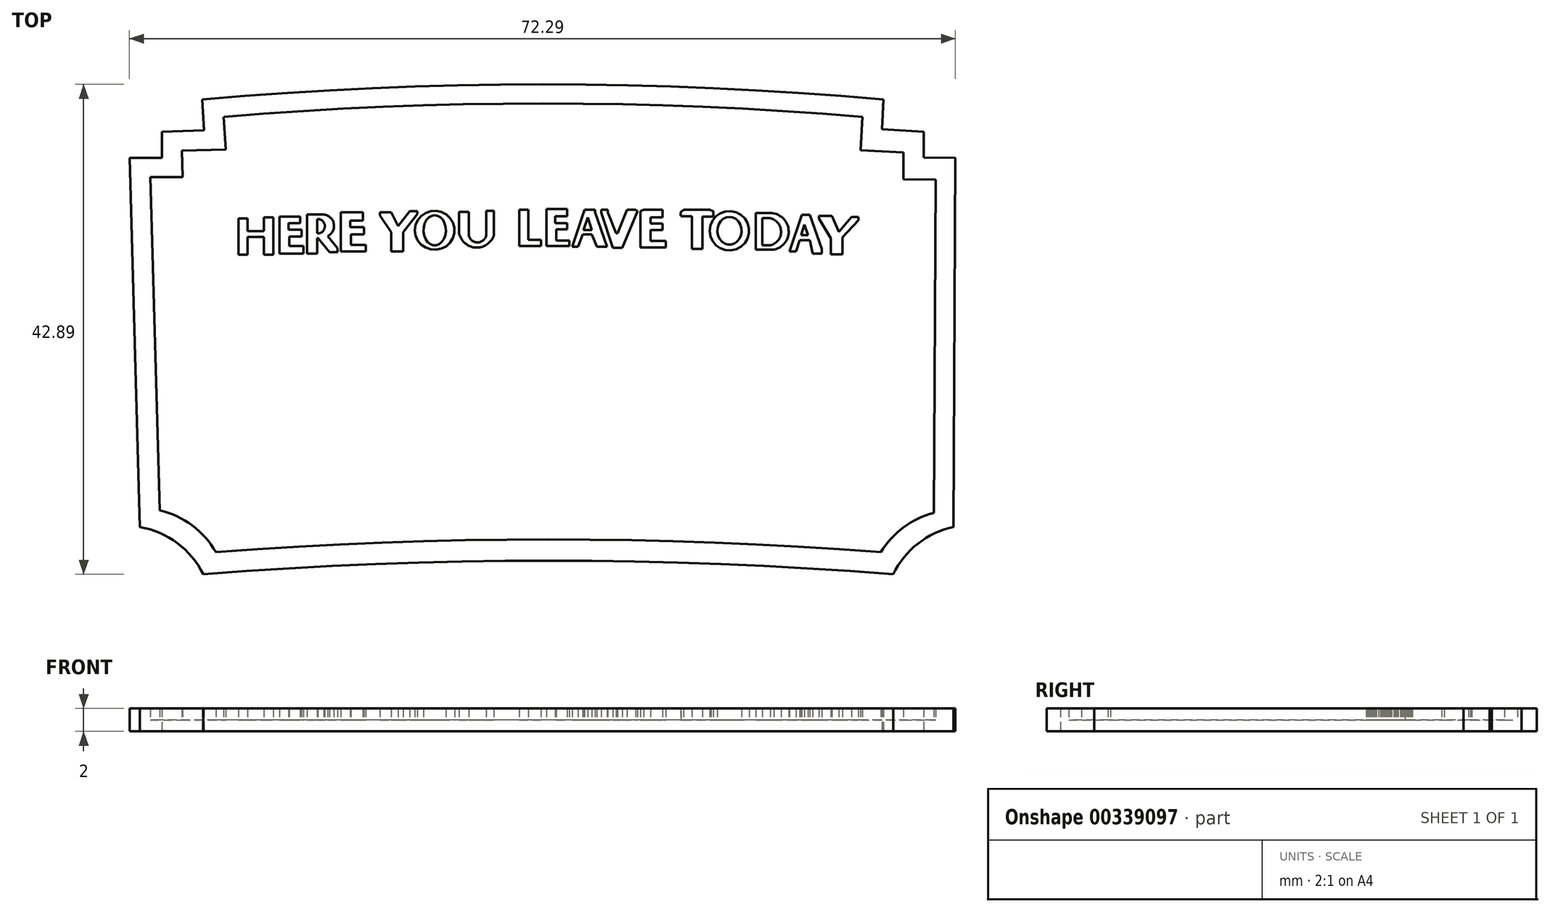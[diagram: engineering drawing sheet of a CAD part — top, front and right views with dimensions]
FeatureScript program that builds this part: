
annotation { "Feature Type Name" : "Feature", "Feature Type Description" : "" }
export const myFeature = defineFeature(function(context is Context, id is Id, definition is map)
    precondition{}
    {
        {
            var Q0;
            Q0=qCreatedBy(makeId("Top.planeOp"),FACE);
            var sketch = newSketch(context, id + "F0", { "sketchPlane" : qUnion([Q0])});
            skLineSegment(sketch, "E0", {"start": v(-33.38, 11.8) * mm, "end": v(-34.3, 44.11) * mm});
            skLineSegment(sketch, "E1", {"start": v(-34.3, 44.11) * mm, "end": v(-31.45, 44.11) * mm});
            skLineSegment(sketch, "E2", {"start": v(37.82, 11.8) * mm, "end": v(37.99, 44.11) * mm});
            skLineSegment(sketch, "E3", {"start": v(37.99, 44.11) * mm, "end": v(35.23, 44.13) * mm});
            skLineSegment(sketch, "E4", {"start": v(-31.45, 44.11) * mm, "end": v(-31.45, 46.4) * mm});
            skLineSegment(sketch, "E5", {"start": v(35.23, 44.13) * mm, "end": v(35.23, 46.4) * mm});
            skLineSegment(sketch, "E6", {"start": v(35.23, 46.4) * mm, "end": v(31.55, 46.6) * mm});
            skLineSegment(sketch, "E7", {"start": v(-27.78, 46.51) * mm, "end": v(-27.93, 49.22) * mm});
            skLineSegment(sketch, "E8", {"start": v(31.55, 46.6) * mm, "end": v(31.7, 49.22) * mm});
            skArc(sketch, "E9", {"start": v(31.7, 49.22) * mm, "mid": v(1.88, 50.54) * mm, "end": v(-27.93, 49.22) * mm});
            skArc(sketch, "E10", {"start": v(-27.84, 7.65) * mm, "mid": v(-30.12, 10.38) * mm, "end": v(-33.38, 11.8) * mm});
            skArc(sketch, "E11", {"start": v(37.82, 11.8) * mm, "mid": v(34.7, 10.33) * mm, "end": v(32.55, 7.65) * mm});
            skLineSegment(sketch, "E12", {"start": v(-31.65, 13.25) * mm, "end": v(-32.48, 42.43) * mm});
            skLineSegment(sketch, "E13", {"start": v(-32.48, 42.43) * mm, "end": v(-29.65, 42.43) * mm});
            skLineSegment(sketch, "E14", {"start": v(-29.65, 42.43) * mm, "end": v(-29.71, 44.73) * mm});
            skLineSegment(sketch, "E15", {"start": v(-31.45, 46.4) * mm, "end": v(-27.78, 46.51) * mm});
            skLineSegment(sketch, "E16", {"start": v(-29.71, 44.73) * mm, "end": v(-25.88, 44.84) * mm});
            skLineSegment(sketch, "E17", {"start": v(-25.88, 44.84) * mm, "end": v(-26.04, 47.7) * mm});
            skLineSegment(sketch, "E18", {"start": v(29.85, 47.7) * mm, "end": v(29.69, 44.78) * mm});
            skLineSegment(sketch, "E19", {"start": v(29.69, 44.78) * mm, "end": v(33.43, 44.57) * mm});
            skLineSegment(sketch, "E20", {"start": v(33.43, 44.57) * mm, "end": v(33.43, 42.23) * mm});
            skLineSegment(sketch, "E21", {"start": v(33.43, 42.23) * mm, "end": v(36.25, 42.21) * mm});
            skArc(sketch, "E22", {"start": v(32.55, 7.65) * mm, "mid": v(2.35, 8.85) * mm, "end": v(-27.84, 7.65) * mm});
            skLineSegment(sketch, "E23", {"start": v(36.25, 42.21) * mm, "end": v(36.1, 13.02) * mm});
            skArc(sketch, "E24", {"start": v(36.1, 13.02) * mm, "mid": v(33.45, 11.76) * mm, "end": v(31.47, 9.59) * mm});
            skArc(sketch, "E25", {"start": v(-26.73, 9.59) * mm, "mid": v(-28.8, 11.93) * mm, "end": v(-31.65, 13.25) * mm});
            skArc(sketch, "E26", {"start": v(31.47, 9.59) * mm, "mid": v(2.37, 10.7) * mm, "end": v(-26.73, 9.59) * mm});
            skArc(sketch, "E27", {"start": v(29.85, 47.7) * mm, "mid": v(1.9, 48.87) * mm, "end": v(-26.04, 47.7) * mm});
            skSolve(sketch);
        }
        {
            var Q0;
            Q0=makeQuery(id+"F0.imprint","IMPRINT",FACE,{"disambiguationData":[TD([[makeQuery(id+"F0.imprint","IMPRINT",EDGE,{"derivedFrom":sQuery(id+"F0.wireOp",EDGE,"E0")}),-1.0]])]});
            extrude(context, id + "F1", {"entities" : qUnion([Q0]), "depth" : 2 * mm});
        }
        {
            var Q0;
            Q0=makeQuery(id+"F0.imprint","IMPRINT",FACE,{"disambiguationData":[TD([[makeQuery(id+"F0.imprint","IMPRINT",EDGE,{"derivedFrom":sQuery(id+"F0.wireOp",EDGE,"E12")}),-1.0]])]});
            extrude(context, id + "F2", {"entities" : qUnion([Q0]), "operationType" : NewBodyOperationType.ADD, "depth" : 1 * mm});
        }
        {
            var Q0;
            Q0=makeQuery(id+"F2.opExtrude","CAP_FACE",FACE,{"disambiguationData":[OSD([sQuery(id+"F0.wireOp",EDGE,"E12"),sQuery(id+"F0.wireOp",EDGE,"E13"),sQuery(id+"F0.wireOp",EDGE,"E14"),sQuery(id+"F0.wireOp",EDGE,"E16"),sQuery(id+"F0.wireOp",EDGE,"E17"),sQuery(id+"F0.wireOp",EDGE,"E18"),sQuery(id+"F0.wireOp",EDGE,"E19"),sQuery(id+"F0.wireOp",EDGE,"E20"),sQuery(id+"F0.wireOp",EDGE,"E21"),sQuery(id+"F0.wireOp",EDGE,"E23"),sQuery(id+"F0.wireOp",EDGE,"E24"),sQuery(id+"F0.wireOp",EDGE,"E25"),sQuery(id+"F0.wireOp",EDGE,"E26"),sQuery(id+"F0.wireOp",EDGE,"E27")])],"isStart":false});
            var sketch = newSketch(context, id + "F3", { "sketchPlane" : qUnion([Q0])});
            skLineSegment(sketch, "E28", {"start": v(-24.76, 35.62) * mm, "end": v(-24.76, 38.81) * mm});
            skLineSegment(sketch, "E29", {"start": v(-24.76, 38.81) * mm, "end": v(-23.95, 38.81) * mm});
            skLineSegment(sketch, "E30", {"start": v(-23.95, 38.81) * mm, "end": v(-23.95, 37.68) * mm});
            skLineSegment(sketch, "E31", {"start": v(-23.95, 37.68) * mm, "end": v(-22.54, 37.68) * mm});
            skLineSegment(sketch, "E32", {"start": v(-22.54, 37.68) * mm, "end": v(-22.54, 38.9) * mm});
            skLineSegment(sketch, "E33", {"start": v(-22.54, 38.9) * mm, "end": v(-21.7, 38.9) * mm});
            skLineSegment(sketch, "E34", {"start": v(-21.7, 38.9) * mm, "end": v(-21.7, 35.64) * mm});
            skLineSegment(sketch, "E35", {"start": v(-21.7, 35.64) * mm, "end": v(-22.53, 35.64) * mm});
            skLineSegment(sketch, "E36", {"start": v(-22.53, 35.64) * mm, "end": v(-22.53, 37.2) * mm});
            skLineSegment(sketch, "E37", {"start": v(-22.53, 37.2) * mm, "end": v(-23.95, 37.2) * mm});
            skLineSegment(sketch, "E38", {"start": v(-23.95, 37.2) * mm, "end": v(-23.95, 35.62) * mm});
            skLineSegment(sketch, "E39", {"start": v(-23.95, 35.62) * mm, "end": v(-24.76, 35.62) * mm});
            skLineSegment(sketch, "E40", {"start": v(-21.16, 35.73) * mm, "end": v(-21.16, 38.97) * mm});
            skLineSegment(sketch, "E41", {"start": v(-21.16, 38.97) * mm, "end": v(-19.35, 38.97) * mm});
            skLineSegment(sketch, "E42", {"start": v(-19.35, 38.97) * mm, "end": v(-19.35, 38.4) * mm});
            skLineSegment(sketch, "E43", {"start": v(-19.35, 38.4) * mm, "end": v(-20.37, 38.4) * mm});
            skLineSegment(sketch, "E44", {"start": v(-20.37, 38.4) * mm, "end": v(-20.37, 37.82) * mm});
            skLineSegment(sketch, "E45", {"start": v(-20.37, 37.82) * mm, "end": v(-19.23, 37.82) * mm});
            skLineSegment(sketch, "E46", {"start": v(-19.23, 37.82) * mm, "end": v(-19.23, 37.23) * mm});
            skLineSegment(sketch, "E47", {"start": v(-19.23, 37.23) * mm, "end": v(-20.31, 37.23) * mm});
            skLineSegment(sketch, "E48", {"start": v(-20.31, 37.23) * mm, "end": v(-20.31, 36.38) * mm});
            skLineSegment(sketch, "E49", {"start": v(-20.31, 36.38) * mm, "end": v(-19.07, 36.38) * mm});
            skLineSegment(sketch, "E50", {"start": v(-19.07, 36.38) * mm, "end": v(-19.07, 35.73) * mm});
            skLineSegment(sketch, "E51", {"start": v(-19.07, 35.73) * mm, "end": v(-21.16, 35.73) * mm});
            skLineSegment(sketch, "E52", {"start": v(-18.75, 35.73) * mm, "end": v(-18.75, 39.15) * mm});
            skLineSegment(sketch, "E53", {"start": v(-18.75, 39.15) * mm, "end": v(-17.29, 39.15) * mm});
            skLineSegment(sketch, "E54", {"start": v(-16.95, 37.25) * mm, "end": v(-16.1, 36.2) * mm});
            skLineSegment(sketch, "E55", {"start": v(-16.1, 36.2) * mm, "end": v(-16.1, 35.85) * mm});
            skLineSegment(sketch, "E56", {"start": v(-16.1, 35.85) * mm, "end": v(-16.77, 35.85) * mm});
            skLineSegment(sketch, "E57", {"start": v(-16.77, 35.85) * mm, "end": v(-17.8, 37.1) * mm});
            skLineSegment(sketch, "E58", {"start": v(-17.8, 37.1) * mm, "end": v(-17.88, 37.1) * mm});
            skLineSegment(sketch, "E59", {"start": v(-17.88, 37.1) * mm, "end": v(-17.88, 35.73) * mm});
            skLineSegment(sketch, "E60", {"start": v(-17.88, 35.73) * mm, "end": v(-18.75, 35.73) * mm});
            skLineSegment(sketch, "E61", {"start": v(-17.88, 37.5) * mm, "end": v(-17.88, 38.75) * mm});
            skArc(sketch, "E62", {"start": v(-17.88, 37.5) * mm, "mid": v(-17.2, 38.12) * mm, "end": v(-17.88, 38.75) * mm});
            skArc(sketch, "E63", {"start": v(-16.95, 37.25) * mm, "mid": v(-16.4, 38.32) * mm, "end": v(-17.29, 39.15) * mm});
            skLineSegment(sketch, "E64", {"start": v(-15.8, 35.92) * mm, "end": v(-15.8, 39.33) * mm});
            skLineSegment(sketch, "E65", {"start": v(-15.8, 39.33) * mm, "end": v(-13.87, 39.33) * mm});
            skLineSegment(sketch, "E66", {"start": v(-13.87, 39.33) * mm, "end": v(-13.87, 38.6) * mm});
            skLineSegment(sketch, "E67", {"start": v(-13.87, 38.6) * mm, "end": v(-14.99, 38.6) * mm});
            skLineSegment(sketch, "E68", {"start": v(-14.99, 38.6) * mm, "end": v(-14.99, 38.03) * mm});
            skLineSegment(sketch, "E69", {"start": v(-14.99, 38.03) * mm, "end": v(-13.76, 38.03) * mm});
            skLineSegment(sketch, "E70", {"start": v(-13.76, 38.03) * mm, "end": v(-13.76, 37.42) * mm});
            skLineSegment(sketch, "E71", {"start": v(-13.76, 37.42) * mm, "end": v(-14.9, 37.42) * mm});
            skLineSegment(sketch, "E72", {"start": v(-14.9, 37.42) * mm, "end": v(-14.9, 36.49) * mm});
            skLineSegment(sketch, "E73", {"start": v(-14.9, 36.49) * mm, "end": v(-13.6, 36.49) * mm});
            skLineSegment(sketch, "E74", {"start": v(-13.6, 36.49) * mm, "end": v(-13.6, 35.92) * mm});
            skLineSegment(sketch, "E75", {"start": v(-13.6, 35.92) * mm, "end": v(-15.8, 35.92) * mm});
            skLineSegment(sketch, "E76", {"start": v(-11.39, 39.33) * mm, "end": v(-10.79, 38.12) * mm});
            skLineSegment(sketch, "E77", {"start": v(-10.79, 38.12) * mm, "end": v(-9.79, 39.43) * mm});
            skLineSegment(sketch, "E78", {"start": v(-9.79, 39.43) * mm, "end": v(-9.11, 39.43) * mm});
            skLineSegment(sketch, "E79", {"start": v(-9.11, 39.43) * mm, "end": v(-9.11, 39.2) * mm});
            skLineSegment(sketch, "E80", {"start": v(-9.11, 39.2) * mm, "end": v(-10.33, 37.6) * mm});
            skLineSegment(sketch, "E81", {"start": v(-10.33, 37.6) * mm, "end": v(-10.33, 35.91) * mm});
            skLineSegment(sketch, "E82", {"start": v(-10.33, 35.91) * mm, "end": v(-11.38, 35.91) * mm});
            skLineSegment(sketch, "E83", {"start": v(-11.38, 35.91) * mm, "end": v(-11.38, 37.6) * mm});
            skLineSegment(sketch, "E84", {"start": v(-11.38, 37.6) * mm, "end": v(-12.37, 39.08) * mm});
            skLineSegment(sketch, "E85", {"start": v(-12.37, 39.08) * mm, "end": v(-12.37, 39.33) * mm});
            skLineSegment(sketch, "E86", {"start": v(-12.37, 39.33) * mm, "end": v(-11.39, 39.33) * mm});
            skEllipse(sketch, "E87", {"center": v(-7.58, 37.77) * mm, "majorRadius": 1.32 * mm, "minorRadius": 0.98 * mm, "majorAxis": v(0, 1)});
            skEllipse(sketch, "E88", {"center": v(-7.58, 37.77) * mm, "majorRadius": 1.7 * mm, "minorRadius": 1.74 * mm, "majorAxis": v(0, 1)});
            skArc(sketch, "E89", {"start": v(-4.6, 37.35) * mm, "mid": v(-3.81, 36.7) * mm, "end": v(-3.06, 37.4) * mm});
            skLineSegment(sketch, "E90", {"start": v(-4.6, 37.35) * mm, "end": v(-4.6, 39.37) * mm});
            skLineSegment(sketch, "E91", {"start": v(-4.6, 39.37) * mm, "end": v(-5.46, 39.37) * mm});
            skLineSegment(sketch, "E92", {"start": v(-5.46, 39.37) * mm, "end": v(-5.46, 37.64) * mm});
            skLineSegment(sketch, "E93", {"start": v(-3.06, 37.4) * mm, "end": v(-3.06, 39.46) * mm});
            skLineSegment(sketch, "E94", {"start": v(-3.06, 39.46) * mm, "end": v(-2.4, 39.46) * mm});
            skLineSegment(sketch, "E95", {"start": v(-2.4, 39.46) * mm, "end": v(-2.4, 37.33) * mm});
            skArc(sketch, "E96", {"start": v(-5.46, 37.64) * mm, "mid": v(-4.05, 36.26) * mm, "end": v(-2.4, 37.33) * mm});
            skLineSegment(sketch, "E97", {"start": v(-0.2, 39.56) * mm, "end": v(-0.2, 36.4) * mm});
            skLineSegment(sketch, "E98", {"start": v(-0.2, 36.4) * mm, "end": v(1.7, 36.4) * mm});
            skLineSegment(sketch, "E99", {"start": v(1.7, 36.4) * mm, "end": v(1.7, 36.94) * mm});
            skLineSegment(sketch, "E100", {"start": v(1.7, 36.94) * mm, "end": v(0.62, 36.94) * mm});
            skLineSegment(sketch, "E101", {"start": v(0.62, 36.94) * mm, "end": v(0.62, 39.56) * mm});
            skLineSegment(sketch, "E102", {"start": v(0.62, 39.56) * mm, "end": v(-0.2, 39.56) * mm});
            skLineSegment(sketch, "E103", {"start": v(4.02, 39) * mm, "end": v(2.97, 39) * mm});
            skLineSegment(sketch, "E104", {"start": v(2.97, 39) * mm, "end": v(2.97, 38.4) * mm});
            skLineSegment(sketch, "E105", {"start": v(2.97, 38.4) * mm, "end": v(4.02, 38.4) * mm});
            skLineSegment(sketch, "E106", {"start": v(4.02, 38.4) * mm, "end": v(4.02, 37.85) * mm});
            skLineSegment(sketch, "E107", {"start": v(4.02, 37.85) * mm, "end": v(3.06, 37.85) * mm});
            skLineSegment(sketch, "E108", {"start": v(3.06, 37.85) * mm, "end": v(3.06, 36.87) * mm});
            skLineSegment(sketch, "E109", {"start": v(3.06, 36.87) * mm, "end": v(4.2, 36.87) * mm});
            skLineSegment(sketch, "E110", {"start": v(4.2, 36.87) * mm, "end": v(4.2, 36.4) * mm});
            skLineSegment(sketch, "E111", {"start": v(4.2, 36.4) * mm, "end": v(2.21, 36.4) * mm});
            skLineSegment(sketch, "E112", {"start": v(4.02, 39) * mm, "end": v(4.02, 39.64) * mm});
            skLineSegment(sketch, "E113", {"start": v(4.02, 39.64) * mm, "end": v(2.21, 39.64) * mm});
            skLineSegment(sketch, "E114", {"start": v(2.21, 39.64) * mm, "end": v(2.21, 36.4) * mm});
            skLineSegment(sketch, "E115", {"start": v(4.58, 36.33) * mm, "end": v(4.97, 36.33) * mm});
            skLineSegment(sketch, "E116", {"start": v(4.97, 36.33) * mm, "end": v(5.39, 37.4) * mm});
            skLineSegment(sketch, "E117", {"start": v(5.39, 37.4) * mm, "end": v(6.17, 37.4) * mm});
            skLineSegment(sketch, "E118", {"start": v(6.17, 37.4) * mm, "end": v(6.63, 36.33) * mm});
            skLineSegment(sketch, "E119", {"start": v(6.63, 36.33) * mm, "end": v(7.5, 36.33) * mm});
            skLineSegment(sketch, "E120", {"start": v(7.5, 36.33) * mm, "end": v(6.45, 39.34) * mm});
            skLineSegment(sketch, "E121", {"start": v(6.45, 39.34) * mm, "end": v(6.45, 39.58) * mm});
            skLineSegment(sketch, "E122", {"start": v(6.45, 39.58) * mm, "end": v(5.53, 39.58) * mm});
            skLineSegment(sketch, "E123", {"start": v(5.53, 39.58) * mm, "end": v(4.46, 36.33) * mm});
            skLineSegment(sketch, "E124", {"start": v(4.46, 36.33) * mm, "end": v(4.58, 36.33) * mm});
            skLineSegment(sketch, "E125", {"start": v(5.53, 37.8) * mm, "end": v(6.17, 37.8) * mm});
            skLineSegment(sketch, "E126", {"start": v(6.17, 37.8) * mm, "end": v(5.8, 38.9) * mm});
            skLineSegment(sketch, "E127", {"start": v(5.8, 38.9) * mm, "end": v(5.44, 37.8) * mm});
            skLineSegment(sketch, "E128", {"start": v(5.44, 37.8) * mm, "end": v(5.53, 37.8) * mm});
            skLineSegment(sketch, "E129", {"start": v(7, 39.58) * mm, "end": v(7, 39.33) * mm});
            skLineSegment(sketch, "E130", {"start": v(7, 39.33) * mm, "end": v(8, 36.23) * mm});
            skLineSegment(sketch, "E131", {"start": v(8, 36.23) * mm, "end": v(8.84, 36.23) * mm});
            skLineSegment(sketch, "E132", {"start": v(8.84, 36.23) * mm, "end": v(10.18, 39.45) * mm});
            skLineSegment(sketch, "E133", {"start": v(10.18, 39.45) * mm, "end": v(10.02, 39.58) * mm});
            skLineSegment(sketch, "E134", {"start": v(10.02, 39.58) * mm, "end": v(9.24, 39.58) * mm});
            skLineSegment(sketch, "E135", {"start": v(9.24, 39.58) * mm, "end": v(8.44, 37.51) * mm});
            skLineSegment(sketch, "E136", {"start": v(8.44, 37.51) * mm, "end": v(8.28, 37.51) * mm});
            skLineSegment(sketch, "E137", {"start": v(8.28, 37.51) * mm, "end": v(7.58, 39.36) * mm});
            skLineSegment(sketch, "E138", {"start": v(7.58, 39.36) * mm, "end": v(7.58, 39.58) * mm});
            skLineSegment(sketch, "E139", {"start": v(7.58, 39.58) * mm, "end": v(7, 39.58) * mm});
            skLineSegment(sketch, "E140", {"start": v(10.43, 36.26) * mm, "end": v(10.43, 39.45) * mm});
            skLineSegment(sketch, "E141", {"start": v(10.43, 39.45) * mm, "end": v(10.7, 39.56) * mm});
            skLineSegment(sketch, "E142", {"start": v(10.7, 39.56) * mm, "end": v(12.36, 39.56) * mm});
            skLineSegment(sketch, "E143", {"start": v(12.36, 39.56) * mm, "end": v(12.36, 38.9) * mm});
            skLineSegment(sketch, "E144", {"start": v(12.36, 38.9) * mm, "end": v(11.3, 38.9) * mm});
            skLineSegment(sketch, "E145", {"start": v(11.3, 38.9) * mm, "end": v(11.3, 38.35) * mm});
            skLineSegment(sketch, "E146", {"start": v(11.3, 38.35) * mm, "end": v(12.35, 38.35) * mm});
            skLineSegment(sketch, "E147", {"start": v(12.35, 38.35) * mm, "end": v(12.35, 37.8) * mm});
            skLineSegment(sketch, "E148", {"start": v(12.35, 37.8) * mm, "end": v(11.3, 37.8) * mm});
            skLineSegment(sketch, "E149", {"start": v(11.3, 37.8) * mm, "end": v(11.3, 36.84) * mm});
            skLineSegment(sketch, "E150", {"start": v(11.3, 36.84) * mm, "end": v(12.64, 36.84) * mm});
            skLineSegment(sketch, "E151", {"start": v(12.64, 36.84) * mm, "end": v(12.64, 36.26) * mm});
            skLineSegment(sketch, "E152", {"start": v(12.64, 36.26) * mm, "end": v(10.43, 36.26) * mm});
            skLineSegment(sketch, "E153", {"start": v(14.94, 36.26) * mm, "end": v(14.94, 39) * mm});
            skLineSegment(sketch, "E154", {"start": v(14.94, 39) * mm, "end": v(14.02, 39) * mm});
            skLineSegment(sketch, "E155", {"start": v(14.02, 39) * mm, "end": v(14.02, 39.4) * mm});
            skLineSegment(sketch, "E156", {"start": v(14.02, 39.4) * mm, "end": v(14.35, 39.53) * mm});
            skLineSegment(sketch, "E157", {"start": v(14.35, 39.53) * mm, "end": v(16.56, 39.53) * mm});
            skLineSegment(sketch, "E158", {"start": v(16.56, 39.53) * mm, "end": v(16.81, 39.43) * mm});
            skLineSegment(sketch, "E159", {"start": v(16.81, 39.43) * mm, "end": v(16.81, 39) * mm});
            skLineSegment(sketch, "E160", {"start": v(16.81, 39) * mm, "end": v(15.8, 39) * mm});
            skLineSegment(sketch, "E161", {"start": v(15.8, 39) * mm, "end": v(15.8, 36.26) * mm});
            skLineSegment(sketch, "E162", {"start": v(15.8, 36.26) * mm, "end": v(14.94, 36.26) * mm});
            skSolve(sketch);
        }
        {
            var Q0;
            Q0=makeQuery(id+"F3.imprint","IMPRINT",FACE,{"disambiguationData":[TD([[makeQuery(id+"F3.imprint","IMPRINT",EDGE,{"derivedFrom":sQuery(id+"F3.wireOp",EDGE,"E28")}),1.0]])]});
            var sketch = newSketch(context, id + "F4", { "sketchPlane" : qUnion([Q0])});
            skLineSegment(sketch, "E163", {"start": v(14.92, 36.15) * mm, "end": v(14.92, 39.04) * mm});
            skLineSegment(sketch, "E164", {"start": v(14.92, 39.04) * mm, "end": v(13.94, 39.04) * mm});
            skLineSegment(sketch, "E165", {"start": v(13.94, 39.04) * mm, "end": v(13.94, 39.35) * mm});
            skLineSegment(sketch, "E166", {"start": v(13.94, 39.35) * mm, "end": v(14.2, 39.57) * mm});
            skLineSegment(sketch, "E167", {"start": v(14.2, 39.57) * mm, "end": v(16.56, 39.57) * mm});
            skLineSegment(sketch, "E168", {"start": v(16.56, 39.57) * mm, "end": v(16.8, 39.33) * mm});
            skLineSegment(sketch, "E169", {"start": v(16.8, 39.33) * mm, "end": v(16.8, 38.96) * mm});
            skLineSegment(sketch, "E170", {"start": v(16.8, 38.96) * mm, "end": v(15.85, 38.96) * mm});
            skLineSegment(sketch, "E171", {"start": v(15.85, 38.96) * mm, "end": v(15.85, 36.15) * mm});
            skLineSegment(sketch, "E172", {"start": v(15.85, 36.15) * mm, "end": v(14.92, 36.15) * mm});
            skEllipse(sketch, "E173", {"center": v(18.22, 37.72) * mm, "majorRadius": 1.22 * mm, "minorRadius": 1.05 * mm, "majorAxis": v(0, 1)});
            skEllipse(sketch, "E174", {"center": v(18.22, 37.72) * mm, "majorRadius": 1.72 * mm, "minorRadius": 1.73 * mm, "majorAxis": v(0, 1)});
            skLineSegment(sketch, "E175", {"start": v(20.52, 39.29) * mm, "end": v(21.47, 39.29) * mm});
            skLineSegment(sketch, "E176", {"start": v(20.52, 36.07) * mm, "end": v(21.47, 36.07) * mm});
            skLineSegment(sketch, "E177", {"start": v(20.52, 36.07) * mm, "end": v(20.52, 39.29) * mm});
            skLineSegment(sketch, "E178", {"start": v(21.47, 36.07) * mm, "end": v(22.11, 36.07) * mm});
            skLineSegment(sketch, "E179", {"start": v(21.47, 39.29) * mm, "end": v(21.77, 39.29) * mm});
            skArc(sketch, "E180", {"start": v(22.11, 36.07) * mm, "mid": v(23.4, 37.83) * mm, "end": v(21.77, 39.29) * mm});
            skLineSegment(sketch, "E181", {"start": v(21.1, 36.46) * mm, "end": v(21.1, 38.85) * mm});
            skLineSegment(sketch, "E182", {"start": v(21.1, 38.85) * mm, "end": v(21.52, 38.85) * mm});
            skLineSegment(sketch, "E183", {"start": v(21.1, 36.46) * mm, "end": v(21.8, 36.46) * mm});
            skArc(sketch, "E184", {"start": v(21.8, 36.46) * mm, "mid": v(22.73, 37.78) * mm, "end": v(21.52, 38.85) * mm});
            skLineSegment(sketch, "E185", {"start": v(23.47, 35.9) * mm, "end": v(24.54, 39.14) * mm});
            skLineSegment(sketch, "E186", {"start": v(24.54, 39.14) * mm, "end": v(25.27, 39.14) * mm});
            skLineSegment(sketch, "E187", {"start": v(25.27, 39.14) * mm, "end": v(26.3, 36.15) * mm});
            skLineSegment(sketch, "E188", {"start": v(26.3, 36.15) * mm, "end": v(26.3, 35.73) * mm});
            skLineSegment(sketch, "E189", {"start": v(26.3, 35.73) * mm, "end": v(25.5, 35.73) * mm});
            skLineSegment(sketch, "E190", {"start": v(25.5, 35.73) * mm, "end": v(25.27, 36.9) * mm});
            skLineSegment(sketch, "E191", {"start": v(25.27, 36.9) * mm, "end": v(24.37, 36.9) * mm});
            skLineSegment(sketch, "E192", {"start": v(24.37, 36.9) * mm, "end": v(24.04, 35.9) * mm});
            skLineSegment(sketch, "E193", {"start": v(24.04, 35.9) * mm, "end": v(23.47, 35.9) * mm});
            skLineSegment(sketch, "E194", {"start": v(24.48, 37.36) * mm, "end": v(24.78, 38.26) * mm});
            skLineSegment(sketch, "E195", {"start": v(24.78, 38.26) * mm, "end": v(25.1, 37.36) * mm});
            skLineSegment(sketch, "E196", {"start": v(25.1, 37.36) * mm, "end": v(24.48, 37.36) * mm});
            skLineSegment(sketch, "E197", {"start": v(27.1, 35.67) * mm, "end": v(27.1, 37.07) * mm});
            skLineSegment(sketch, "E198", {"start": v(27.1, 37.07) * mm, "end": v(26.05, 38.81) * mm});
            skLineSegment(sketch, "E199", {"start": v(26.05, 38.81) * mm, "end": v(26.05, 39.03) * mm});
            skLineSegment(sketch, "E200", {"start": v(26.05, 39.03) * mm, "end": v(27.2, 39.03) * mm});
            skLineSegment(sketch, "E201", {"start": v(27.2, 39.03) * mm, "end": v(27.8, 37.64) * mm});
            skLineSegment(sketch, "E202", {"start": v(27.8, 37.64) * mm, "end": v(28.91, 38.92) * mm});
            skLineSegment(sketch, "E203", {"start": v(28.91, 38.92) * mm, "end": v(29.49, 38.92) * mm});
            skLineSegment(sketch, "E204", {"start": v(29.49, 38.92) * mm, "end": v(29.49, 38.66) * mm});
            skLineSegment(sketch, "E205", {"start": v(29.49, 38.66) * mm, "end": v(28.11, 37.14) * mm});
            skLineSegment(sketch, "E206", {"start": v(28.11, 37.14) * mm, "end": v(28.11, 35.67) * mm});
            skLineSegment(sketch, "E207", {"start": v(28.11, 35.67) * mm, "end": v(27.1, 35.67) * mm});
            skSolve(sketch);
        }
        {
            var Q0;
            Q0 = qSketchRegion(id + "F3", true);
            var Q1;
            Q1 = qSketchRegion(id + "F4", true);
            extrude(context, id + "F5", {"entities" : qUnion([Q0, Q1]), "operationType" : NewBodyOperationType.ADD, "depth" : 1 * mm});
        }
    });
